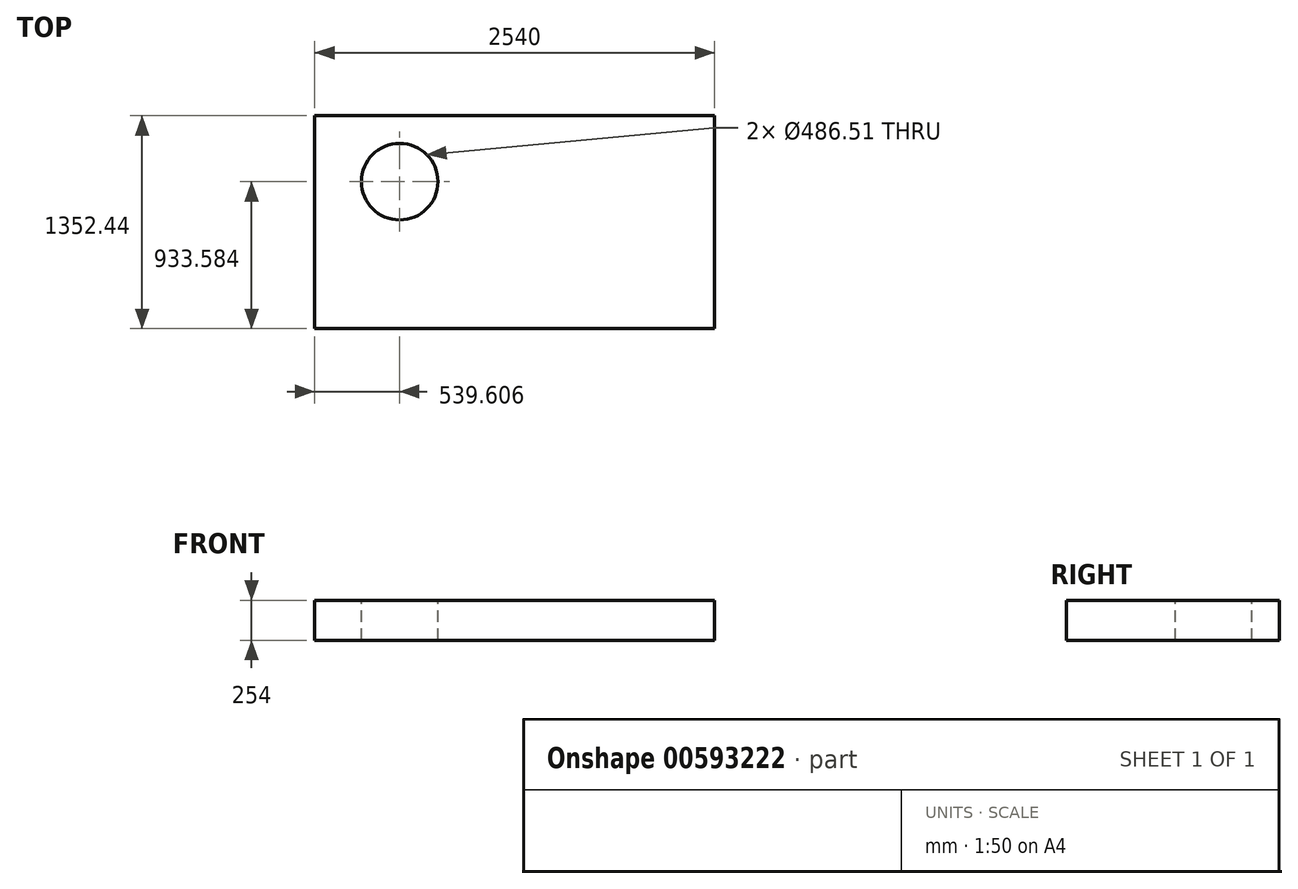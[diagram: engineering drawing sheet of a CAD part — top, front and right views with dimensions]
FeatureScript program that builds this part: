
annotation { "Feature Type Name" : "Feature", "Feature Type Description" : "" }
export const myFeature = defineFeature(function(context is Context, id is Id, definition is map)
    precondition{}
    {
        {
            var Q0;
            Q0=qCreatedBy(makeId("Top.planeOp"),FACE);
            var sketch = newSketch(context, id + "F0", { "sketchPlane" : qUnion([Q0])});
            skLineSegment(sketch, "E0.bottom", {"start": v(1270, 676.22) * mm, "end": v(-1270, 676.22) * mm});
            skLineSegment(sketch, "E0.top", {"start": v(1270, -676.22) * mm, "end": v(-1270, -676.22) * mm});
            skLineSegment(sketch, "E0.left", {"start": v(1270, 676.22) * mm, "end": v(1270, -676.22) * mm});
            skLineSegment(sketch, "E0.right", {"start": v(-1270, 676.22) * mm, "end": v(-1270, -676.22) * mm});
            skPoint(sketch, "E0.middle", {"position": v(0, 0) * mm});
            skSolve(sketch);
        }
        {
            var Q0;
            Q0 = qSketchRegion(id + "F0", true);
            extrude(context, id + "F1", {"entities" : qUnion([Q0]), "endBound" : BoundingType.SYMMETRIC, "depth" : 254 * mm, "offsetDistance" : 25.4 * mm});
        }
        {
            var Q0;
            Q0=makeQuery(id+"F1.opExtrude","CAP_FACE",FACE,{"disambiguationData":[OSD([sQuery(id+"F0.wireOp",EDGE,"E0.bottom"),sQuery(id+"F0.wireOp",EDGE,"E0.top"),sQuery(id+"F0.wireOp",EDGE,"E0.left"),sQuery(id+"F0.wireOp",EDGE,"E0.right")])],"isStart":false});
            var sketch = newSketch(context, id + "F2", { "sketchPlane" : qUnion([Q0])});
            skCircle(sketch, "E1", {"center": v(-730.4, 257.36) * mm, "radius": 243.26 * mm});
            skSolve(sketch);
        }
        {
            var Q0;
            Q0 = qSketchRegion(id + "F2", true);
            extrude(context, id + "F3", {"entities" : qUnion([Q0]), "operationType" : NewBodyOperationType.REMOVE, "endBound" : BoundingType.THROUGH_ALL, "oppositeDirection" : true, "depth" : 25.4 * mm, "offsetDistance" : 25.4 * mm});
        }
    });
